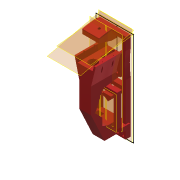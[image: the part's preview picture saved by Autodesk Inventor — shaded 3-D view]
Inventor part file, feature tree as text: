
AUTODESK INVENTOR PART (.ipt)
format: ipt  version: 2019.4 (Build 234330000, 330)  size: 562,688 bytes
history: native  units: mm
features: extrude x14, sketch x13, reference x13, projected_geometry x13, plane x7, other x7, mirror x1
ambient origin geometry x8: Origin, YZ Plane, XZ Plane, XY Plane, X Axis, Y Axis, Z Axis, Center Point
bodies: Solid1 (feature_tree)
feature tree (68):
  plane  "Work Plane1"
  extrude  "Extrusion1"  Depth=14.0mm
  plane  "Work Plane2"
  extrude  "Extrusion2"  Depth=4.0mm
  extrude  "Extrusion3"  Depth=5.0mm TaperAngle=0.0deg
  plane  "Work Plane3"
  extrude  "Extrusion4"  Depth=0.5mm
  sketch  "Sketch5"  dims[d25=5.0mm d26=0.5mm]
  extrude  "Extrusion5"  Depth=5.0mm
  extrude  "Extrusion6"  Depth=5.0mm TaperAngle=0.0deg
  extrude  "Extrusion7"  Depth=3.0mm
  extrude  "Extrusion8"  Depth=5.0mm
  extrude  "Extrusion9"  Depth=12.0mm
  extrude  "Extrusion10"  Depth=17.0mm
  extrude  "Extrusion11"  Depth=0.15mm
  mirror  "Mirror2"
  extrude  "Extrusion18"  Depth=5.0mm TaperAngle=0.0deg
  extrude  "Extrusion21"  Depth=10.0mm
  plane  "Work Plane10"
  extrude  "Extrusion22"  Depth=10.0mm
  sketch  "Sketch24"  dims[d47=0.5mm d48=0.5mm d49=1.5mm d50=90.0deg d51=0.2mm d52=5.0mm d53=0.0mm d54=5.0mm d55=0.0mm d56=3.5mm d57=2.5mm d58=5.0mm d59=0.0mm d60=0.0mm d61=0.0mm d62=0.0mm d63=12.0mm d64=8.0mm d65=2.9mm d66=2.9mm d67=2.9mm d68=2.9mm d69=0.1mm d70=20.071286mm d71=22.0mm d72=6.0mm d73=6.0mm d74=7.0mm d75=0.0mm d76=5.0mm d77=0.0mm d78=10.0mm d79=1.9mm d80=1.9mm d81=5.0mm d82=0.0mm d83=2.9mm d84=2.9mm d85=5.0mm d86=2.9mm d87=5.0mm d88=0.0mm d99=2.9mm d111=10.0mm d112=0.0mm d119=20.0mm d120=0.0mm d121=2.9mm d122=2.6mm d123=20.0mm d124=0.0mm]
  sketch  "Sketch1"  dims[d2=3.0mm d9=6.0mm d10=0.0mm d19=14.0mm]
  reference  "Reference1"
  reference  "Reference2"
  reference  "Reference3"
  reference  "Reference4"
  sketch  "Sketch2"  dims[d20=4.0mm d21=4.0mm]
  projected_geometry  "Projected Loop1"
  projected_geometry  "Projected Loop2"
  projected_geometry  "Projected Loop3"
  projected_geometry  "Projected Loop4"
  sketch  "Sketch4"  dims[d22=5.0mm d23=5.0mm d24=0.0mm]
  projected_geometry  "Projected Loop5"
  reference  "Reference5"
  projected_geometry  "Projected Loop6"
  projected_geometry  "Projected Loop7"
  projected_geometry  "Projected Loop8"
  sketch  "Sketch7"  dims[d27=0.5mm d28=5.0mm]
  reference  "Reference7"
  sketch  "Sketch8"  dims[d29=0.5mm d32=5.0mm d33=0.0mm]
  projected_geometry  "Projected Loop9"
  projected_geometry  "Projected Loop10"
  reference  "Reference8"
  sketch  "Sketch9"  dims[d34=5.0mm d35=3.0mm]
  projected_geometry  "Projected Loop11"
  reference  "Reference9"
  reference  "Reference10"
  sketch  "Sketch10"  dims[d36=8.0mm d37=5.0mm]
  reference  "Reference11"
  reference  "Reference12"
  reference  "Reference13"
  reference  "Reference14"
  sketch  "Sketch12"  dims[d38=3.0mm d39=12.0mm]
  projected_geometry  "Projected Loop12"
  plane  "Work Plane6"
  plane  "Work Plane7"
  sketch  "Sketch19"  dims[d40=0.0mm d41=17.0mm]
  projected_geometry  "Projected Loop16"
  sketch  "Sketch22"  dims[d42=2.0mm d43=0.15mm]
  plane  "Work Plane9"
  sketch  "Sketch23"  dims[d44=45.0deg d45=5.0mm d46=0.0mm]
  other  "Assembly_Opentrons_Autofocus_v1.iam"
  other  "01_Slide_camera_x_v1:1"
  other  "07_OPENTRONS_Autofocus_objectivemount_v0:1"
  other  "00_objectivelens_10x:1"
  other  "00_COMAR_Mirror_10mm:1"
  other  "00_RasPi_Camera:1"
  other  "00_opticalpath:1"
